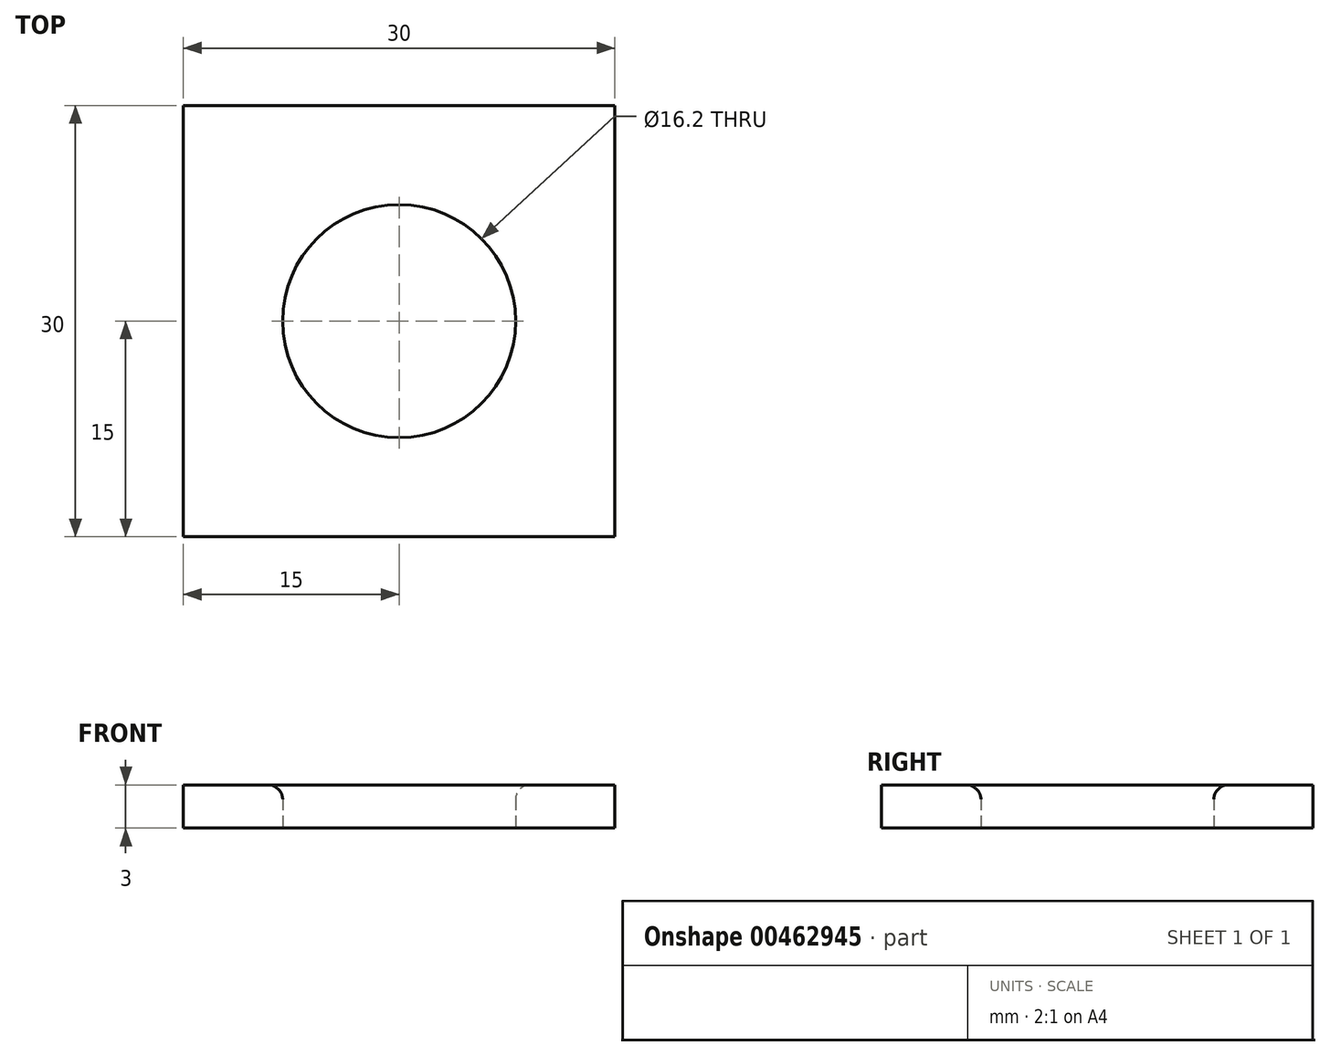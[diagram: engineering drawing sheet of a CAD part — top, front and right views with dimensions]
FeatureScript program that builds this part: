
annotation { "Feature Type Name" : "Feature", "Feature Type Description" : "" }
export const myFeature = defineFeature(function(context is Context, id is Id, definition is map)
    precondition{}
    {
        {
            var Q0;
            Q0=qCreatedBy(makeId("Top.planeOp"),FACE);
            var sketch = newSketch(context, id + "F0", { "sketchPlane" : qUnion([Q0])});
            skLineSegment(sketch, "E0.bottom", {"start": v(15, 15) * mm, "end": v(-15, 15) * mm});
            skLineSegment(sketch, "E0.top", {"start": v(15, -15) * mm, "end": v(-15, -15) * mm});
            skLineSegment(sketch, "E0.left", {"start": v(15, 15) * mm, "end": v(15, -15) * mm});
            skLineSegment(sketch, "E0.right", {"start": v(-15, 15) * mm, "end": v(-15, -15) * mm});
            skPoint(sketch, "E0.middle", {"position": v(0, 0) * mm});
            skCircle(sketch, "E1", {"center": v(0, 0) * mm, "radius": 8.1 * mm});
            skSolve(sketch);
        }
        {
            var Q0;
            Q0=makeQuery(id+"F0.imprint","IMPRINT",FACE,{"disambiguationData":[TD([[makeQuery(id+"F0.imprint","IMPRINT",EDGE,{"derivedFrom":sQuery(id+"F0.wireOp",EDGE,"E0.bottom")}),1.0]])]});
            extrude(context, id + "F1", {"entities" : qUnion([Q0]), "depth" : 3 * mm});
        }
        {
            var Q0;
            Q0=makeQuery(id+"F1.opExtrude","CAP_EDGE",EDGE,{"disambiguationData":[OSD([sQuery(id+"F0.wireOp",EDGE,"E1")])],"isStart":false});
            fillet(context, id + "F2", {"entities" : qUnion([Q0]), "radius" : 1 * mm, "tangentPropagation" : true, "allowEdgeOverflow" : false});
        }
    });
